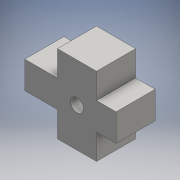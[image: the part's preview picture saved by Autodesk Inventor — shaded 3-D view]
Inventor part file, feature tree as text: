
AUTODESK INVENTOR PART (.ipt)
format: ipt  version: 2016 (Build 200138000, 138)  size: 105,472 bytes
history: native  units: mm
features: other x3, extrude x1, hole x1
ambient origin geometry x8: Origin, YZ Plane, XZ Plane, XY Plane, X Axis, Y Axis, Z Axis, Center Point
bodies: Solid1 (feature_tree)
feature tree (5):
  other  "zero_sketch.ipt"
  extrude  "Extrusion1"  Depth=10.0mm
  hole  "Hole1"  [1 undecoded]
  other  "base+body"
  other  "base+body_1"
note: 1 required parameter value undecoded (feature->parameter linkage not recoverable at this tier; creation-order binding heuristic only, values carry confidence <= 0.55)
